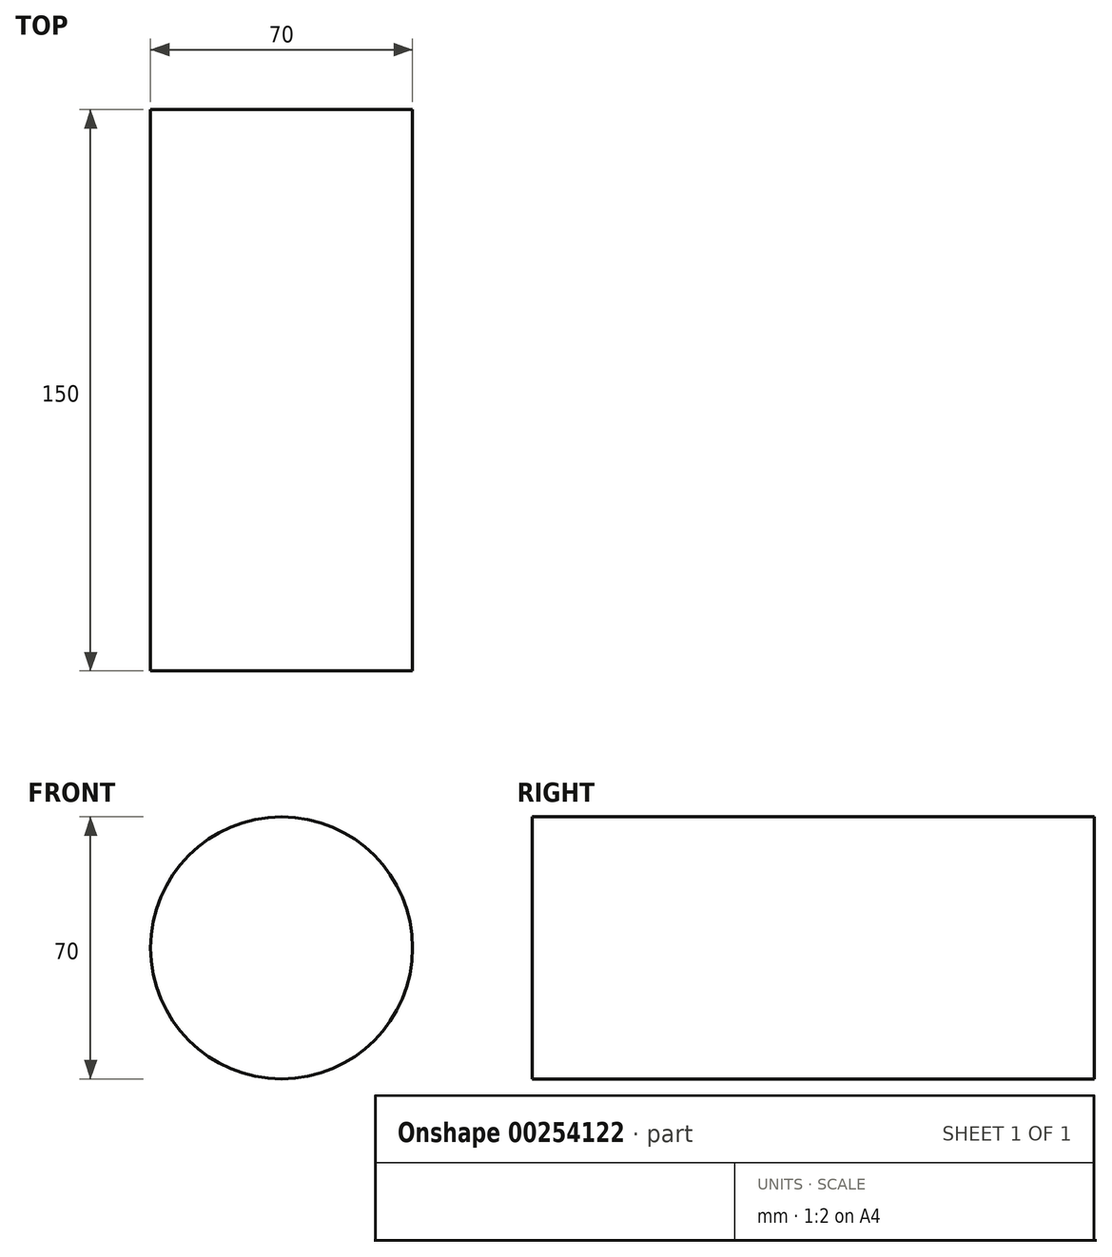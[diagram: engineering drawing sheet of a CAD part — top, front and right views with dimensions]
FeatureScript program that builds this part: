
annotation { "Feature Type Name" : "Feature", "Feature Type Description" : "" }
export const myFeature = defineFeature(function(context is Context, id is Id, definition is map)
    precondition{}
    {
        {
            var Q0;
            Q0=qCreatedBy(makeId("Front.planeOp"),FACE);
            var sketch = newSketch(context, id + "F0", { "sketchPlane" : qUnion([Q0])});
            skCircle(sketch, "E0", {"center": v(0, 0) * mm, "radius": 35 * mm});
            skSolve(sketch);
        }
        {
            var Q0;
            Q0 = qSketchRegion(id + "F0", true);
            extrude(context, id + "F1", {"entities" : qUnion([Q0]), "depth" : 150 * mm, "offsetDistance" : 25 * mm});
        }
    });
